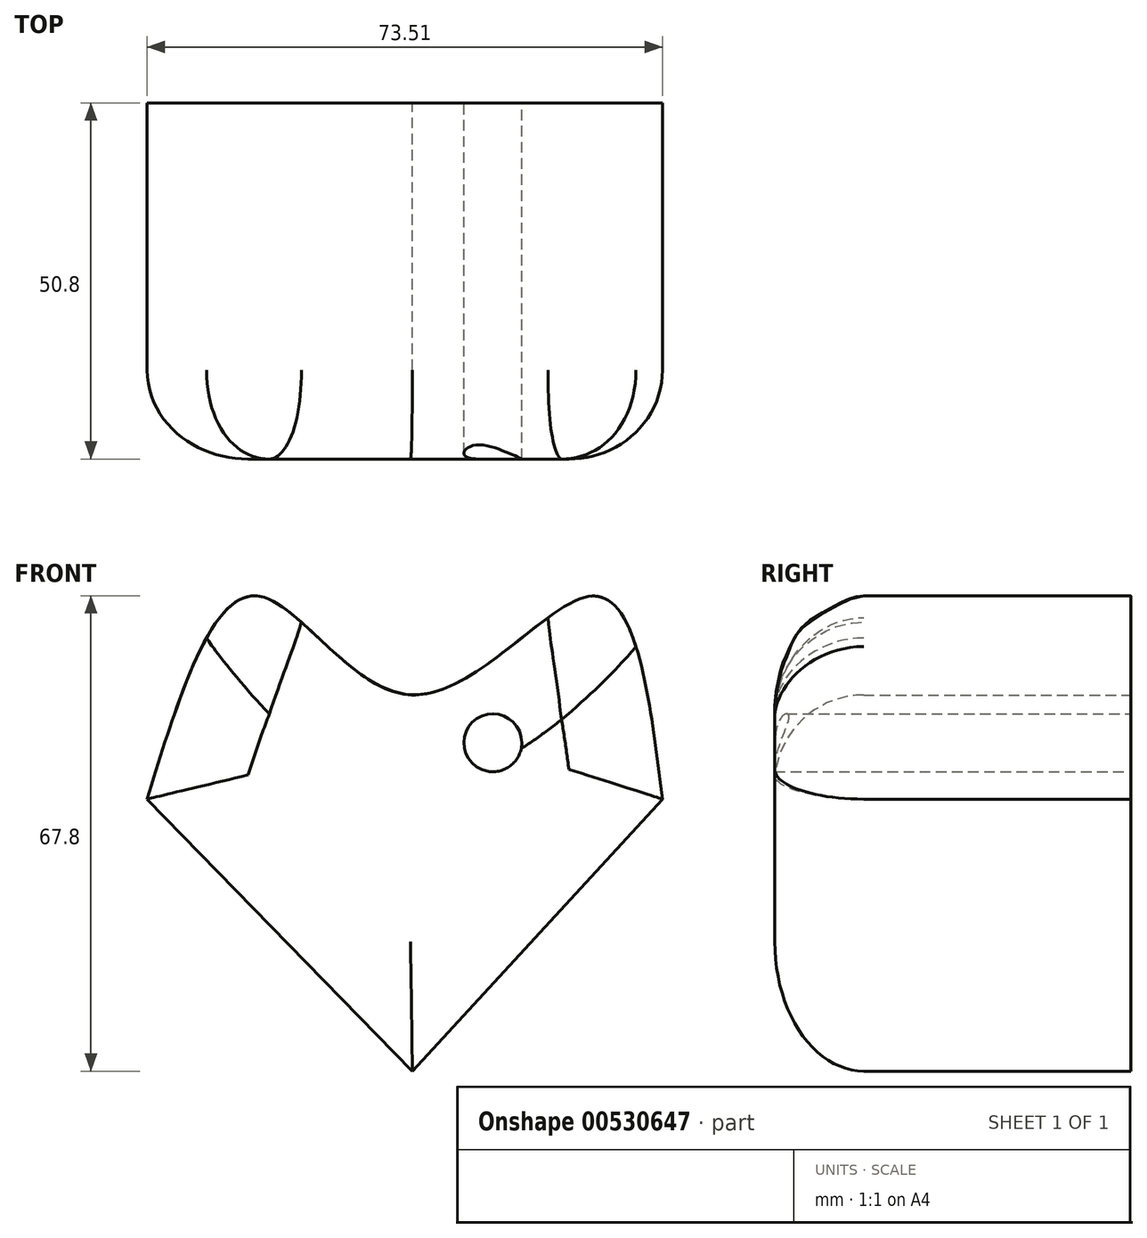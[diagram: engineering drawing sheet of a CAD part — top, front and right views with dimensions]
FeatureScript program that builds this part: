
annotation { "Feature Type Name" : "Feature", "Feature Type Description" : "" }
export const myFeature = defineFeature(function(context is Context, id is Id, definition is map)
    precondition{}
    {
        {
            var Q0;
            Q0=qCreatedBy(makeId("Front.planeOp"),FACE);
            var sketch = newSketch(context, id + "F0", { "sketchPlane" : qUnion([Q0])});
            skLineSegment(sketch, "E0", {"start": v(0, 0) * mm, "end": v(-37.84, 38.8) * mm});
            skLineSegment(sketch, "E1", {"start": v(0, 0) * mm, "end": v(35.67, 38.8) * mm});
            skFitSpline(sketch, "E2", {"points": [v(-37.84, 38.8) * mm, v(-22.03, 67.77) * mm, v(0, 53.66) * mm, v(25.78, 67.77) * mm, v(35.67, 38.8) * mm], "startDerivative": vector(52.34, 169.55) * mm, "endDerivative": vector(21.32, -172.11) * mm});
            skSolve(sketch);
        }
        {
            var Q0;
            Q0=makeQuery(id+"F0.imprint","IMPRINT",FACE,{"disambiguationData":[TD([[makeQuery(id+"F0.imprint","IMPRINT",EDGE,{"derivedFrom":sQuery(id+"F0.wireOp",EDGE,"E0")}),-1.0]])]});
            extrude(context, id + "F1", {"entities" : qUnion([Q0]), "depth" : 50.8 * mm, "offsetDistance" : 25.4 * mm});
        }
        {
            var Q0;
            Q0=makeQuery(id+"F1.opExtrude","CAP_FACE",FACE,{"disambiguationData":[OSD([sQuery(id+"F0.wireOp",EDGE,"E0"),sQuery(id+"F0.wireOp",EDGE,"E1"),sQuery(id+"F0.wireOp",EDGE,"E2")])],"isStart":false});
            fillet(context, id + "F2", {"entities" : qUnion([Q0]), "radius" : 12.7 * mm, "tangentPropagation" : true, "allowEdgeOverflow" : false});
        }
        {
            var Q0;
            Q0=makeQuery(id+"F0.imprint","IMPRINT",FACE,{"disambiguationData":[TD([[makeQuery(id+"F0.imprint","IMPRINT",EDGE,{"derivedFrom":sQuery(id+"F0.wireOp",EDGE,"E0")}),-1.0]])]});
            var sketch = newSketch(context, id + "F3", { "sketchPlane" : qUnion([Q0])});
            skCircle(sketch, "E3.cCircle", {"center": v(0, 46.04) * mm, "radius": 2.54 * mm, "construction": true});
            skLineSegment(sketch, "E3.0", {"start": v(-2.54, 41.64) * mm, "end": v(-2.54, 50.44) * mm});
            skLineSegment(sketch, "E3.1", {"start": v(-2.54, 50.44) * mm, "end": v(5.08, 46.04) * mm});
            skLineSegment(sketch, "E3.2", {"start": v(5.08, 46.04) * mm, "end": v(-2.54, 41.64) * mm});
            skPoint(sketch, "E3.0.midPoint", {"position": v(-2.54, 46.04) * mm});
            skSolve(sketch);
        }
        {
            var Q0;
            Q0 = qSketchRegion(id + "F3", true);
            extrude(context, id + "F4", {"entities" : qUnion([Q0]), "operationType" : NewBodyOperationType.REMOVE, "endBound" : BoundingType.THROUGH_ALL, "oppositeDirection" : true, "depth" : 25.4 * mm, "offsetDistance" : 25.4 * mm});
        }
        {
            var Q0;
            Q0=makeQuery(id+"F0.imprint","IMPRINT",FACE,{"disambiguationData":[TD([[makeQuery(id+"F0.imprint","IMPRINT",EDGE,{"derivedFrom":sQuery(id+"F0.wireOp",EDGE,"E0")}),-1.0]])]});
            var sketch = newSketch(context, id + "F5", { "sketchPlane" : qUnion([Q0])});
            skCircle(sketch, "E4", {"center": v(11.47, 46.84) * mm, "radius": 4.14 * mm});
            skSolve(sketch);
        }
        {
            var Q0;
            Q0 = qSketchRegion(id + "F5", true);
            extrude(context, id + "F6", {"entities" : qUnion([Q0]), "operationType" : NewBodyOperationType.REMOVE, "endBound" : BoundingType.THROUGH_ALL, "depth" : 25.4 * mm, "offsetDistance" : 25.4 * mm});
        }
    });
